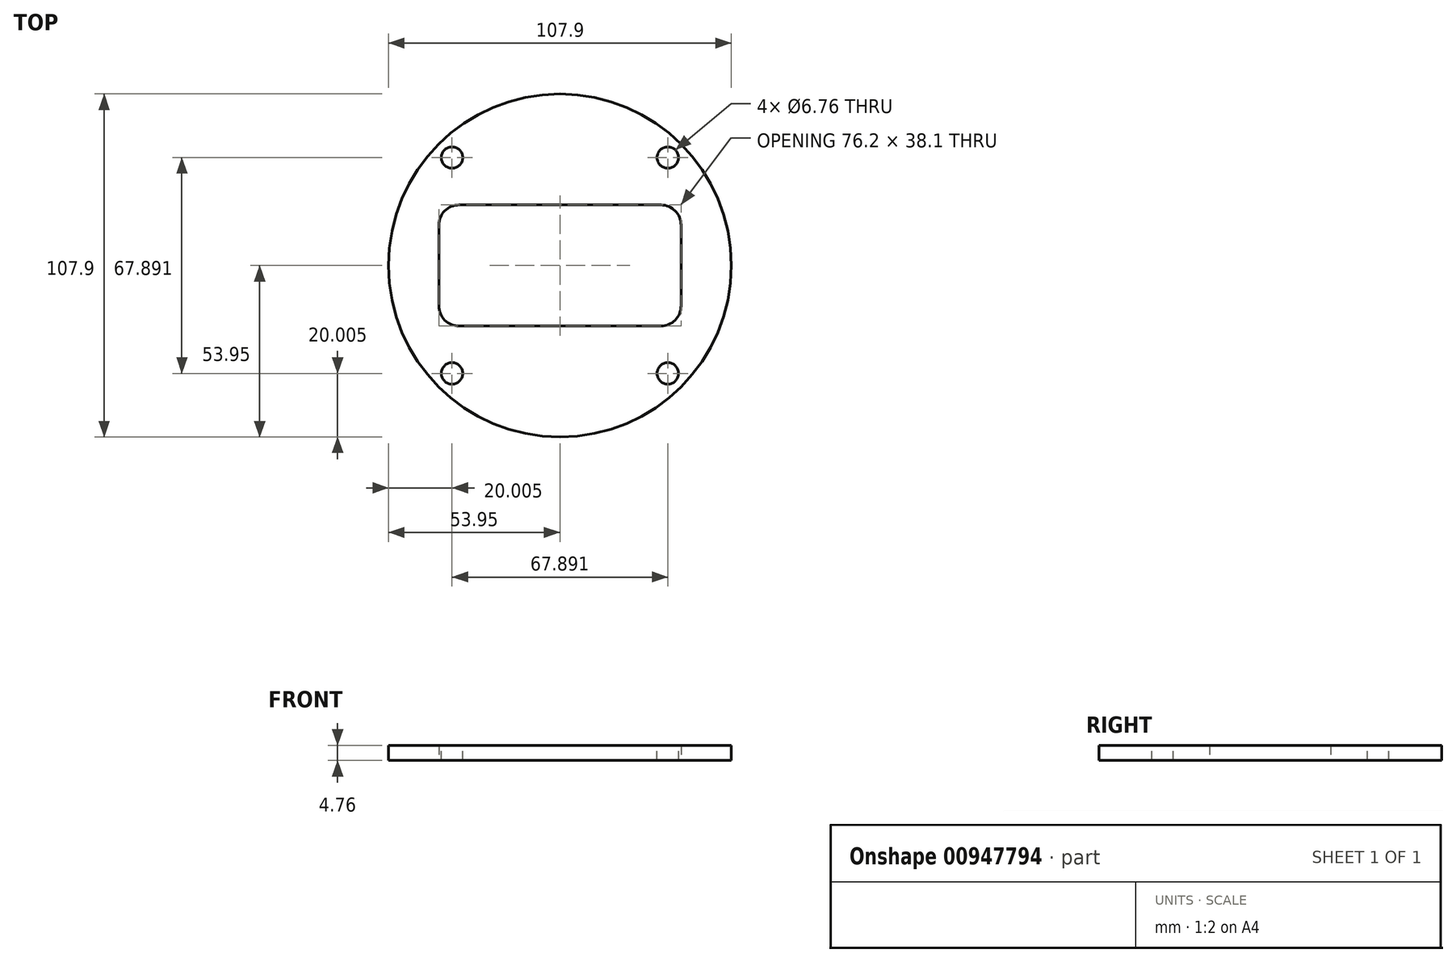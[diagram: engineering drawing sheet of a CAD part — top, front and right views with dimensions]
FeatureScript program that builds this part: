
annotation { "Feature Type Name" : "Feature", "Feature Type Description" : "" }
export const myFeature = defineFeature(function(context is Context, id is Id, definition is map)
    precondition{}
    {
        {
            var Q0;
            Q0=qCreatedBy(makeId("Top.planeOp"),FACE);
            var sketch = newSketch(context, id + "F0", { "sketchPlane" : qUnion([Q0])});
            skCircle(sketch, "E0", {"center": v(0, 0) * mm, "radius": 53.95 * mm});
            skLineSegment(sketch, "E1.bottom", {"start": v(31.75, -19.05) * mm, "end": v(-31.75, -19.05) * mm});
            skLineSegment(sketch, "E1.top", {"start": v(31.75, 19.05) * mm, "end": v(-31.75, 19.05) * mm});
            skLineSegment(sketch, "E1.left", {"start": v(38.1, -12.7) * mm, "end": v(38.1, 12.7) * mm});
            skLineSegment(sketch, "E1.right", {"start": v(-38.1, -12.7) * mm, "end": v(-38.1, 12.7) * mm});
            skPoint(sketch, "E2.visualSharp", {"position": v(-38.1, 19.05) * mm});
            skArc(sketch, "E2.filletArc", {"start": v(-31.75, 19.05) * mm, "mid": v(-36.24, 17.2) * mm, "end": v(-38.1, 12.7) * mm});
            skPoint(sketch, "E3.visualSharp", {"position": v(38.1, 19.05) * mm});
            skArc(sketch, "E3.filletArc", {"start": v(38.1, 12.7) * mm, "mid": v(36.24, 17.2) * mm, "end": v(31.75, 19.05) * mm});
            skPoint(sketch, "E4.visualSharp", {"position": v(38.1, -19.05) * mm});
            skArc(sketch, "E4.filletArc", {"start": v(31.75, -19.05) * mm, "mid": v(36.24, -17.2) * mm, "end": v(38.1, -12.7) * mm});
            skPoint(sketch, "E5.visualSharp", {"position": v(-38.1, -19.05) * mm});
            skArc(sketch, "E5.filletArc", {"start": v(-38.1, -12.7) * mm, "mid": v(-36.24, -17.2) * mm, "end": v(-31.75, -19.05) * mm});
            skLineSegment(sketch, "E6", {"start": v(0, 0) * mm, "end": v(33.95, 33.95) * mm, "construction": true});
            skPoint(sketch, "E7", {"position": v(33.95, 33.95) * mm});
            skPoint(sketch, "E8.1.0", {"position": v(-33.95, 33.95) * mm});
            skPoint(sketch, "E8.2.0", {"position": v(-33.95, -33.95) * mm});
            skPoint(sketch, "E8.3.0", {"position": v(33.95, -33.95) * mm});
            skSolve(sketch);
        }
        {
            var Q0;
            Q0 = qSketchRegion(id + "F0", true);
            extrude(context, id + "F1", {"entities" : qUnion([Q0]), "depth" : 4.76 * mm, "offsetDistance" : 25 * mm});
        }
        {
            var Q0;
            Q0=sQuery(id+"F0.wireOp",VERTEX,"E7");
            var Q1;
            Q1=sQuery(id+"F0.wireOp",VERTEX,"E8.1.0");
            var Q2;
            Q2=sQuery(id+"F0.wireOp",VERTEX,"E8.2.0");
            var Q3;
            Q3=sQuery(id+"F0.wireOp",VERTEX,"E8.3.0");
            var Q4;
            Q4=makeQuery(id+"F1.opExtrude","SWEPT_BODY",BODY,{"disambiguationData":[OSD([sQuery(id+"F0.wireOp",EDGE,"E0"),sQuery(id+"F0.wireOp",EDGE,"E1.bottom"),sQuery(id+"F0.wireOp",EDGE,"E1.top"),sQuery(id+"F0.wireOp",EDGE,"E1.left"),sQuery(id+"F0.wireOp",EDGE,"E1.right"),sQuery(id+"F0.wireOp",EDGE,"E2.filletArc"),sQuery(id+"F0.wireOp",EDGE,"E3.filletArc"),sQuery(id+"F0.wireOp",EDGE,"E4.filletArc"),sQuery(id+"F0.wireOp",EDGE,"E5.filletArc")])]});
            hole(context, id + "F2", {"style" : HoleStyle.SIMPLE, "endStyle" : HoleEndStyle.THROUGH, "oppositeDirection" : true, "standardTappedOrClearance" : lookupTablePath({ "fit" : "Close (ASME)", "standard" : "ANSI", "size" : "1/4", "type" : "Clearance" }), "standardBlindInLast" : lookupTablePath({ "fit" : "Close", "standard" : "ANSI", "engagement" : "75%", "pitch" : "20 tpi", "size" : "1/4", "type" : "Clearance & tapped" }), "holeDiameter" : 6.76 * mm, "majorDiameter" : 5 * mm, "isTappedThrough" : true, "tappedDepth" : 40.45 * mm, "tapClearance" : 3, "locations" : qUnion([Q0, Q1, Q2, Q3]), "scope" : qUnion([Q4]), "startStyle" : HoleStartStyle.SKETCH});
        }
    });
